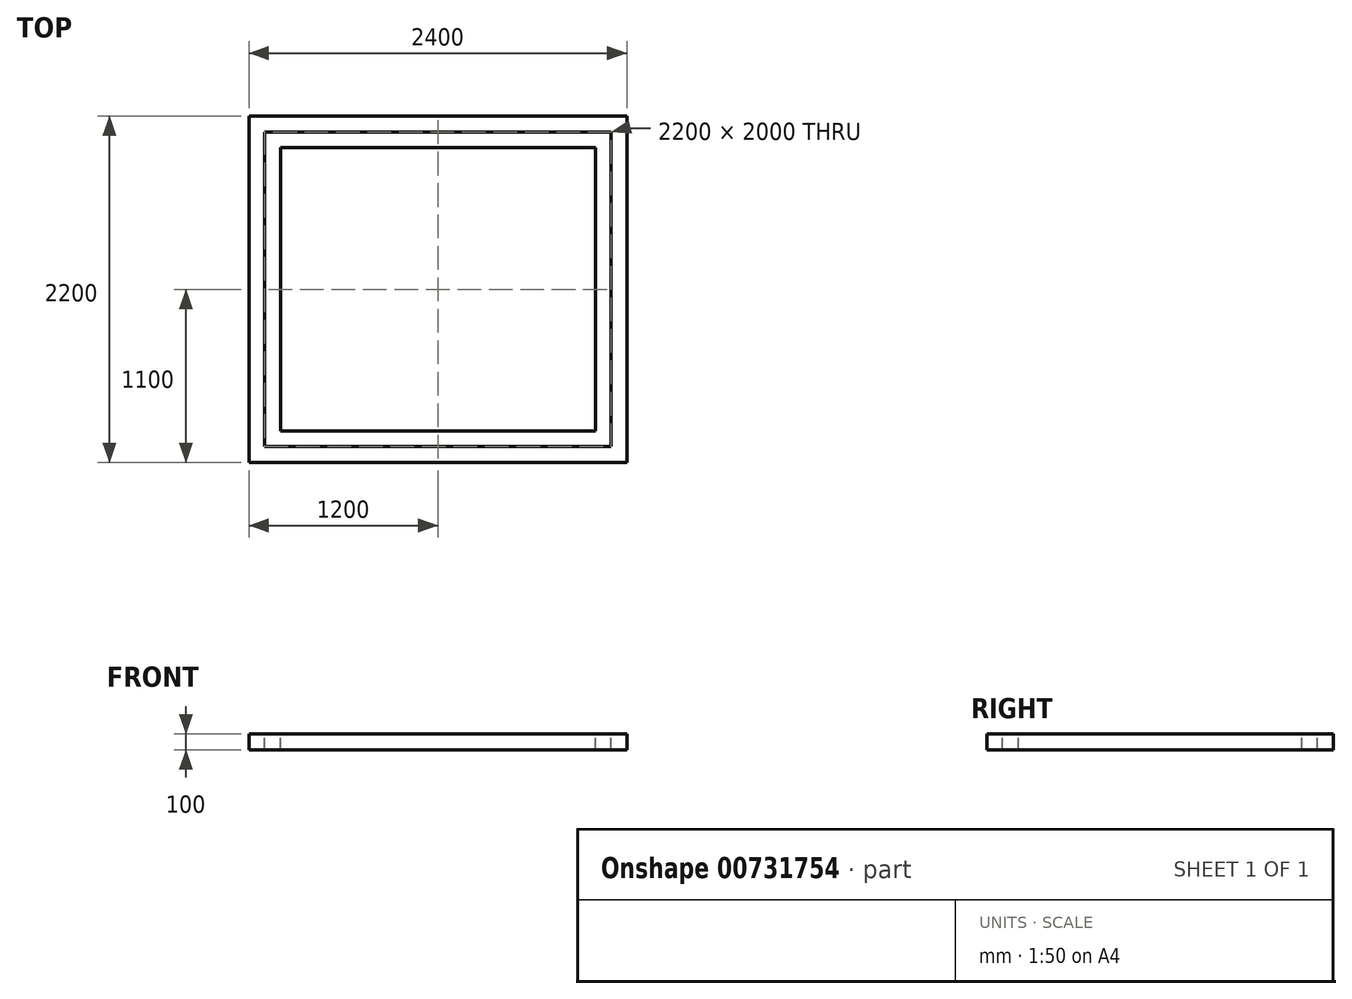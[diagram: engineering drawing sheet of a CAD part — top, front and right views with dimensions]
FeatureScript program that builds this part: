
annotation { "Feature Type Name" : "Feature", "Feature Type Description" : "" }
export const myFeature = defineFeature(function(context is Context, id is Id, definition is map)
    precondition{}
    {
        {
            var Q0;
            Q0=qCreatedBy(makeId("Top.planeOp"),FACE);
            var sketch = newSketch(context, id + "F0", { "sketchPlane" : qUnion([Q0])});
            skLineSegment(sketch, "E0.bottom", {"start": v(1200, -1100) * mm, "end": v(-1200, -1100) * mm});
            skLineSegment(sketch, "E0.top", {"start": v(1200, 1100) * mm, "end": v(-1200, 1100) * mm});
            skLineSegment(sketch, "E0.left", {"start": v(1200, -1100) * mm, "end": v(1200, 1100) * mm});
            skLineSegment(sketch, "E0.right", {"start": v(-1200, -1100) * mm, "end": v(-1200, 1100) * mm});
            skPoint(sketch, "E0.middle", {"position": v(0, 0) * mm});
            skSolve(sketch);
        }
        {
            var Q0;
            Q0=makeQuery(id+"F0.imprint","IMPRINT",FACE,{"disambiguationData":[TD([[makeQuery(id+"F0.imprint","IMPRINT",EDGE,{"derivedFrom":sQuery(id+"F0.wireOp",EDGE,"E0.bottom")}),-1.0]])]});
            extrude(context, id + "F1", {"entities" : qUnion([Q0]), "depth" : 100 * mm, "offsetDistance" : 25 * mm});
        }
        {
            var Q0;
            Q0=makeQuery(id+"F1.opExtrude","CAP_FACE",FACE,{"disambiguationData":[OSD([sQuery(id+"F0.wireOp",EDGE,"E0.bottom"),sQuery(id+"F0.wireOp",EDGE,"E0.top"),sQuery(id+"F0.wireOp",EDGE,"E0.left"),sQuery(id+"F0.wireOp",EDGE,"E0.right")])],"isStart":false});
            var sketch = newSketch(context, id + "F2", { "sketchPlane" : qUnion([Q0])});
            skLineSegment(sketch, "E1.0", {"start": v(1100, -1000) * mm, "end": v(1100, 1000) * mm});
            skLineSegment(sketch, "E1.1", {"start": v(1100, 1000) * mm, "end": v(-1100, 1000) * mm});
            skLineSegment(sketch, "E1.2", {"start": v(-1100, -1000) * mm, "end": v(-1100, 1000) * mm});
            skLineSegment(sketch, "E2.0", {"start": v(1100, -1000) * mm, "end": v(-1100, -1000) * mm});
            skLineSegment(sketch, "E3.0", {"start": v(1000, 900) * mm, "end": v(-1000, 900) * mm});
            skLineSegment(sketch, "E3.1", {"start": v(1000, -900) * mm, "end": v(1000, 900) * mm});
            skLineSegment(sketch, "E3.2", {"start": v(1000, -900) * mm, "end": v(-1000, -900) * mm});
            skLineSegment(sketch, "E3.3", {"start": v(-1000, -900) * mm, "end": v(-1000, 900) * mm});
            skSolve(sketch);
        }
        {
            var Q0;
            Q0=makeQuery(id+"F2.imprint","IMPRINT",FACE,{"disambiguationData":[TD([[makeQuery(id+"F2.imprint","IMPRINT",EDGE,{"derivedFrom":sQuery(id+"F2.wireOp",EDGE,"E1.0")}),1.0]])]});
            extrude(context, id + "F3", {"entities" : qUnion([Q0]), "operationType" : NewBodyOperationType.REMOVE, "endBound" : BoundingType.THROUGH_ALL, "oppositeDirection" : true, "depth" : 0.1 * mm, "offsetDistance" : 25 * mm});
        }
    });
